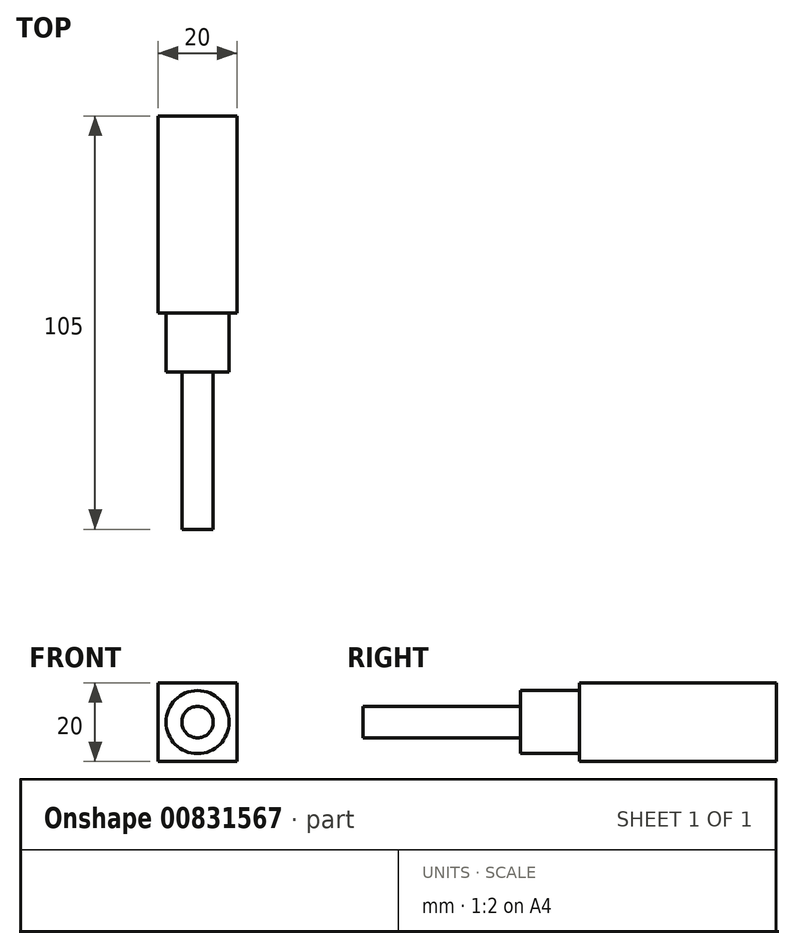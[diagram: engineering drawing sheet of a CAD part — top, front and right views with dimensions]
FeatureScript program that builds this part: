
annotation { "Feature Type Name" : "Feature", "Feature Type Description" : "" }
export const myFeature = defineFeature(function(context is Context, id is Id, definition is map)
    precondition{}
    {
        {
            var Q0;
            Q0=qCreatedBy(makeId("Front.planeOp"),FACE);
            var sketch = newSketch(context, id + "F0", { "sketchPlane" : qUnion([Q0])});
            skLineSegment(sketch, "E0.bottom", {"start": v(0, 0) * mm, "end": v(20, 0) * mm});
            skLineSegment(sketch, "E0.top", {"start": v(0, 20) * mm, "end": v(20, 20) * mm});
            skLineSegment(sketch, "E0.left", {"start": v(0, 0) * mm, "end": v(0, 20) * mm});
            skLineSegment(sketch, "E0.right", {"start": v(20, 0) * mm, "end": v(20, 20) * mm});
            skSolve(sketch);
        }
        {
            var Q0;
            Q0 = qSketchRegion(id + "F0", true);
            var Q1;
            Q1=makeQuery(id+"F0.imprint","IMPRINT",FACE,{"disambiguationData":[TD([[makeQuery(id+"F0.imprint","IMPRINT",EDGE,{"derivedFrom":sQuery(id+"F0.wireOp",EDGE,"E0.bottom")}),1.0]])]});
            extrude(context, id + "F1", {"entities" : qUnion([Q0, Q1]), "depth" : 50 * mm, "offsetDistance" : 25 * mm});
        }
        {
            var Q0;
            Q0=makeQuery(id+"F1.opExtrude","CAP_FACE",FACE,{"disambiguationData":[OSD([sQuery(id+"F0.wireOp",EDGE,"E0.bottom"),sQuery(id+"F0.wireOp",EDGE,"E0.top"),sQuery(id+"F0.wireOp",EDGE,"E0.left"),sQuery(id+"F0.wireOp",EDGE,"E0.right")])],"isStart":false});
            var sketch = newSketch(context, id + "F2", { "sketchPlane" : qUnion([Q0])});
            skPoint(sketch, "E1", {"position": v(10, 10) * mm});
            skPoint(sketch, "E1.positionSnap0", {"position": v(20, 10) * mm});
            skPoint(sketch, "E1.positionSnap1", {"position": v(10, 20) * mm});
            skCircle(sketch, "E2", {"center": v(10, 10) * mm, "radius": 8 * mm});
            skSolve(sketch);
        }
        {
            var Q0;
            Q0 = qSketchRegion(id + "F2", true);
            extrude(context, id + "F3", {"entities" : qUnion([Q0]), "operationType" : NewBodyOperationType.ADD, "depth" : 15 * mm, "offsetDistance" : 25 * mm});
        }
        {
            var Q0;
            Q0=makeQuery(id+"F3.opExtrude","CAP_FACE",FACE,{"disambiguationData":[OSD([sQuery(id+"F2.wireOp",EDGE,"E2")])],"isStart":false});
            var sketch = newSketch(context, id + "F4", { "sketchPlane" : qUnion([Q0])});
            skPoint(sketch, "E3", {"position": v(10, 10) * mm});
            skCircle(sketch, "E4", {"center": v(10, 10) * mm, "radius": 4 * mm});
            skSolve(sketch);
        }
        {
            var Q0;
            Q0 = qSketchRegion(id + "F4", true);
            extrude(context, id + "F5", {"entities" : qUnion([Q0]), "operationType" : NewBodyOperationType.ADD, "depth" : 40 * mm, "offsetDistance" : 25 * mm});
        }
    });
